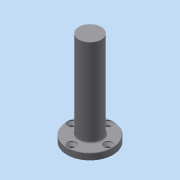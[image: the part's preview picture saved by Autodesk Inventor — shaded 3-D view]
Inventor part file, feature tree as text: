
AUTODESK INVENTOR PART (.ipt)
format: ipt  version: 2013 (Build 170138000, 138)  size: 172,032 bytes
history: native  units: in
note: dims shown in document units (in); Inventor stores cm internally (conversion verified against a paired STEP export)
features: other x1, extrude x1, fillet x1, imported_body x1, sketch x1
ambient origin geometry x8: Origin, YZ Plane, XZ Plane, XY Plane, X Axis, Y Axis, Z Axis, Center Point
feature tree (5):
  other  "UR5 tool standard plade1"
  extrude  "Extrusion1"  Depth=4.7244in TaperAngle=0.0deg
  fillet  "Fillet1"  Radius=0.0787in
  imported_body  "Base1"
  sketch  "Sketch1"  dims[d0=1.2106in d3=4.7244in d4=0.0in d5=0.0787in]
